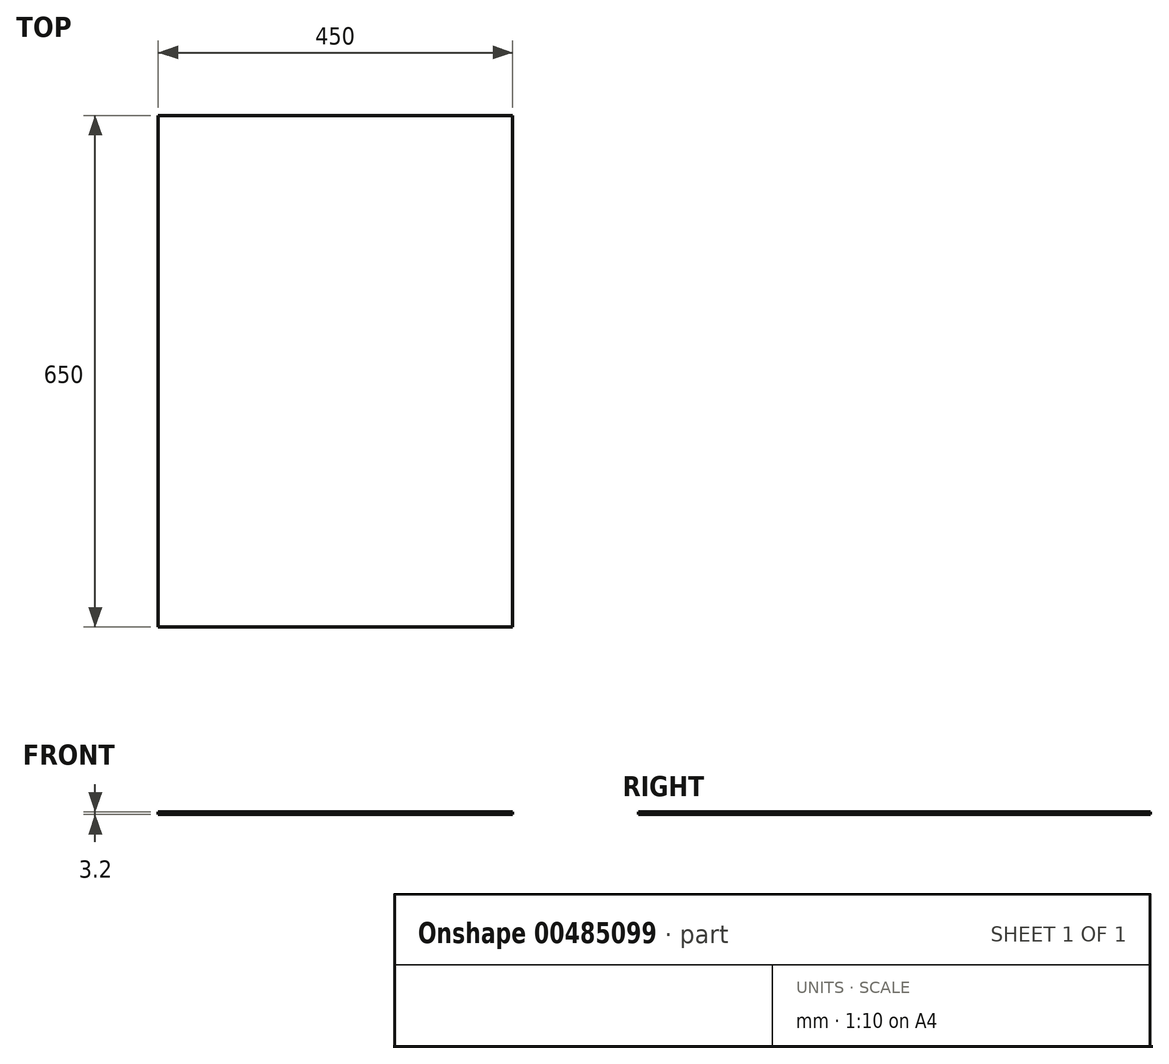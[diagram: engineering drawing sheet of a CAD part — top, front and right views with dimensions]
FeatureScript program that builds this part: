
annotation { "Feature Type Name" : "Feature", "Feature Type Description" : "" }
export const myFeature = defineFeature(function(context is Context, id is Id, definition is map)
    precondition{}
    {
        {
            var Q0;
            Q0=qCreatedBy(makeId("Top.planeOp"),FACE);
            var sketch = newSketch(context, id + "F0", { "sketchPlane" : qUnion([Q0])});
            skLineSegment(sketch, "E0.bottom", {"start": v(-53.37, 621.87) * mm, "end": v(396.63, 621.87) * mm});
            skLineSegment(sketch, "E0.top", {"start": v(-53.37, -28.13) * mm, "end": v(396.63, -28.13) * mm});
            skLineSegment(sketch, "E0.left", {"start": v(-53.37, 621.87) * mm, "end": v(-53.37, -28.13) * mm});
            skLineSegment(sketch, "E0.right", {"start": v(396.63, 621.87) * mm, "end": v(396.63, -28.13) * mm});
            skSolve(sketch);
        }
        {
            var Q0;
            Q0=makeQuery(id+"F0.imprint","IMPRINT",FACE,{"disambiguationData":[TD([[makeQuery(id+"F0.imprint","IMPRINT",EDGE,{"derivedFrom":sQuery(id+"F0.wireOp",EDGE,"E0.bottom")}),-1.0]])]});
            extrude(context, id + "F1", {"entities" : qUnion([Q0]), "depth" : 3.2 * mm, "offsetDistance" : 25 * mm});
        }
    });
